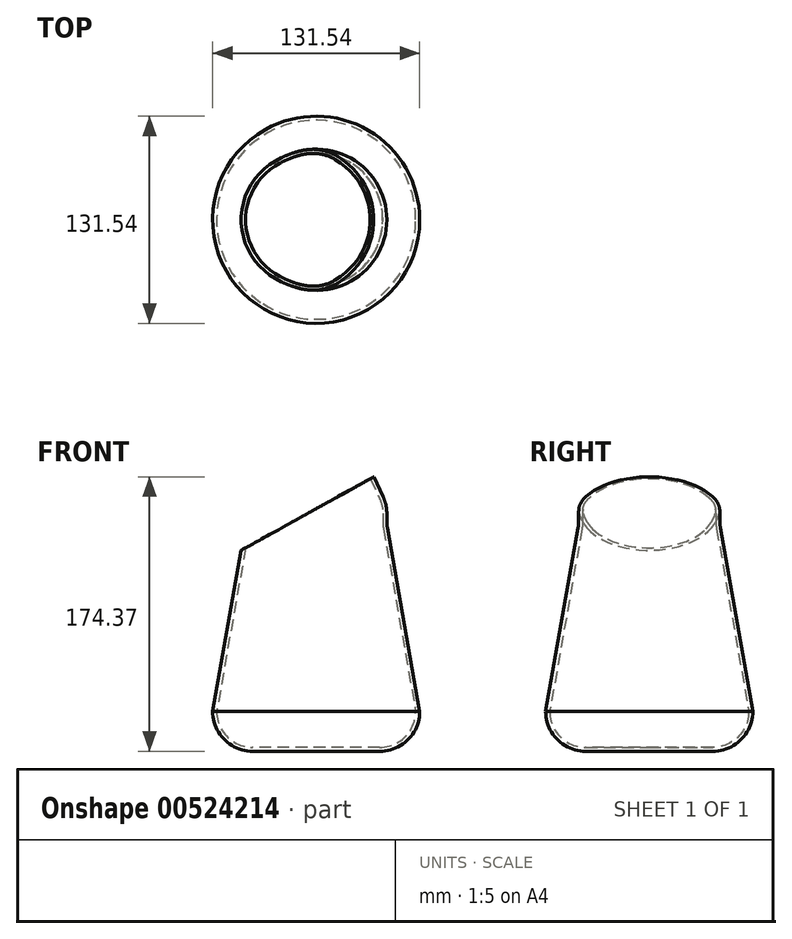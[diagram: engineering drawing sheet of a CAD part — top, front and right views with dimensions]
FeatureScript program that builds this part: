
annotation { "Feature Type Name" : "Feature", "Feature Type Description" : "" }
export const myFeature = defineFeature(function(context is Context, id is Id, definition is map)
    precondition{}
    {
        {
            var Q0;
            Q0=qCreatedBy(makeId("Top.planeOp"),FACE);
            var sketch = newSketch(context, id + "F0", { "sketchPlane" : qUnion([Q0])});
            skCircle(sketch, "E0", {"center": v(0, 0) * mm, "radius": 44.86 * mm});
            skSolve(sketch);
        }
        {
            var Q0;
            Q0 = qSketchRegion(id + "F0", true);
            extrude(context, id + "F1", {"entities" : qUnion([Q0]), "oppositeDirection" : true, "depth" : 118.61 * mm, "offsetDistance" : 25.4 * mm, "hasDraft" : true, "draftAngle" : 10 * degree});
        }
        {
            var Q0;
            Q0=makeQuery(id+"F1.opExtrude","CAP_FACE",FACE,{"disambiguationData":[OSD([sQuery(id+"F0.wireOp",EDGE,"E0")])],"isStart":false});
            extrude(context, id + "F2", {"entities" : qUnion([Q0]), "operationType" : NewBodyOperationType.ADD, "depth" : 25.4 * mm, "offsetDistance" : 25.4 * mm});
        }
        {
            var Q0;
            Q0=makeQuery(id+"F2.opExtrude","CAP_EDGE",EDGE,{"disambiguationData":[OSD([sQuery(id+"F0.wireOp",EDGE,"E0")])],"isStart":false});
            fillet(context, id + "F3", {"entities" : qUnion([Q0]), "radius" : 25.4 * mm, "tangentPropagation" : true, "allowEdgeOverflow" : false});
        }
        {
            var Q0;
            Q0=makeQuery(id+"F1.opExtrude","CAP_FACE",FACE,{"disambiguationData":[OSD([sQuery(id+"F0.wireOp",EDGE,"E0")])],"isStart":true});
            extrude(context, id + "F4", {"entities" : qUnion([Q0]), "operationType" : NewBodyOperationType.ADD, "depth" : 12.7 * mm, "offsetDistance" : 25.4 * mm});
        }
        {
            var Q0;
            Q0=makeQuery(id+"F4.opExtrude","CAP_FACE",FACE,{"disambiguationData":[OSD([sQuery(id+"F0.wireOp",EDGE,"E0")])],"isStart":false});
            extrude(context, id + "F5", {"entities" : qUnion([Q0]), "operationType" : NewBodyOperationType.ADD, "depth" : 23.46 * mm, "offsetDistance" : 25.4 * mm, "hasDraft" : true, "draftAngle" : 25 * degree, "draftPullDirection" : true});
        }
        {
            var Q0;
            {var subQ0=sQuery(id+"F0.wireOp",EDGE,"E0");Q0=makeQuery(id+"F5.boolean.opBoolean","MERGE",EDGE,{"derivedFrom":[makeQuery(id+"F4.opExtrude","CAP_EDGE",EDGE,{"disambiguationData":[OSD([subQ0])],"isStart":false}),makeQuery(id+"F5.opExtrude","CAP_EDGE",EDGE,{"disambiguationData":[OSD([subQ0])],"isStart":true})]});}
            var Q1;
            {var subQ0=sQuery(id+"F0.wireOp",EDGE,"E0");Q1=makeQuery(id+"F4.boolean.opBoolean","MERGE",EDGE,{"derivedFrom":[makeQuery(id+"F1.opExtrude","CAP_EDGE",EDGE,{"disambiguationData":[OSD([subQ0])],"isStart":true}),makeQuery(id+"F4.opExtrude","CAP_EDGE",EDGE,{"disambiguationData":[OSD([subQ0])],"isStart":true})]});}
            fillet(context, id + "F6", {"entities" : qUnion([Q0, Q1]), "radius" : 25.4 * mm, "tangentPropagation" : true, "allowEdgeOverflow" : false});
        }
        {
            var Q0;
            Q0=qCreatedBy(makeId("Front.planeOp"),FACE);
            var sketch = newSketch(context, id + "F7", { "sketchPlane" : qUnion([Q0])});
            skLineSegment(sketch, "E1", {"start": v(-53.71, -19.69) * mm, "end": v(80.52, 54.68) * mm});
            skLineSegment(sketch, "E2", {"start": v(80.52, 54.68) * mm, "end": v(35.96, 135.12) * mm});
            skLineSegment(sketch, "E3", {"start": v(35.96, 135.12) * mm, "end": v(-99.1, 60.3) * mm});
            skLineSegment(sketch, "E4", {"start": v(-53.71, -19.69) * mm, "end": v(-99.1, 60.3) * mm});
            skSolve(sketch);
        }
        {
            var Q0;
            Q0 = qSketchRegion(id + "F7", true);
            extrude(context, id + "F8", {"entities" : qUnion([Q0]), "operationType" : NewBodyOperationType.REMOVE, "endBound" : BoundingType.SYMMETRIC, "oppositeDirection" : true, "depth" : 98.56 * mm, "offsetDistance" : 25.4 * mm});
        }
        {
            var Q0;
            Q0=makeQuery(id+"F8.boolean.opBoolean","COPY",FACE,{"derivedFrom":makeQuery(id+"F8.opExtrude","SWEPT_FACE",FACE,{"disambiguationData":[OSD([sQuery(id+"F7.wireOp",EDGE,"E1")])]})});
            shell(context, id + "F9", {"entities" : qUnion([Q0]), "thickness" : 2.54 * mm});
        }
    });
